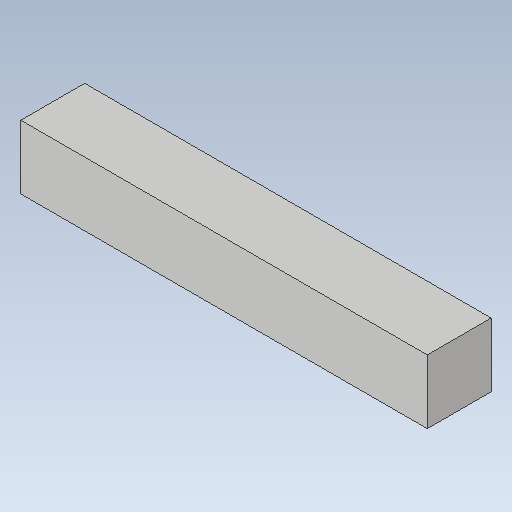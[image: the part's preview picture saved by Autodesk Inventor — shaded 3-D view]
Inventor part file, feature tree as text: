
AUTODESK INVENTOR PART (.ipt)
format: ipt  version: 2020 (Build 240168000, 168)  size: 88,576 bytes
history: native  units: mm
features: other x3, extrude x1, sketch x1, reference x1
ambient origin geometry x8: Origin, YZ Plane, XZ Plane, XY Plane, X Axis, Y Axis, Z Axis, Center Point
bodies: 实体1 (feature_tree)
feature tree (6):
  extrude  "拉伸1"  [1 undecoded]
  sketch  "草图1"  dims[d0=22.0mm d1=0.0mm]
  reference  "参考1"
  other  "<userpath>\Desktop\装配3\Workspace\cpz assemble.iam"
  other  "cpz assemble.iam"
  other  "轴:2"
note: 1 required parameter value undecoded (feature->parameter linkage not recoverable at this tier; creation-order binding heuristic only, values carry confidence <= 0.55)
